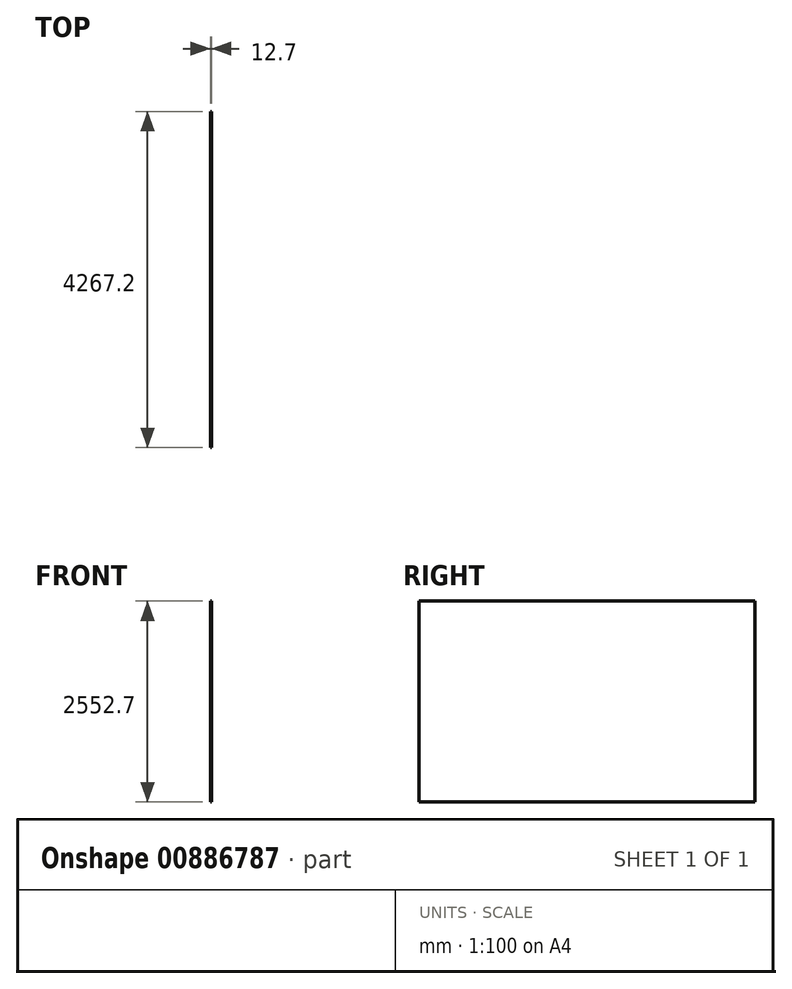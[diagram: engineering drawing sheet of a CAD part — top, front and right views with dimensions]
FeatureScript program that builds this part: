
annotation { "Feature Type Name" : "Feature", "Feature Type Description" : "" }
export const myFeature = defineFeature(function(context is Context, id is Id, definition is map)
    precondition{}
    {
        {
            var Q0;
            Q0=qCreatedBy(makeId("Right.planeOp"),FACE);
            var sketch = newSketch(context, id + "F0", { "sketchPlane" : qUnion([Q0])});
            skLineSegment(sketch, "E0.bottom", {"start": v(-2133.6, 1276.35) * mm, "end": v(2133.6, 1276.35) * mm});
            skLineSegment(sketch, "E0.top", {"start": v(-2133.6, -1276.35) * mm, "end": v(2133.6, -1276.35) * mm});
            skLineSegment(sketch, "E0.left", {"start": v(-2133.6, 1276.35) * mm, "end": v(-2133.6, -1276.35) * mm});
            skLineSegment(sketch, "E0.right", {"start": v(2133.6, 1276.35) * mm, "end": v(2133.6, -1276.35) * mm});
            skPoint(sketch, "E0.middle", {"position": v(0, 0) * mm});
            skSolve(sketch);
        }
        {
            var Q0;
            Q0=qSketchRegion(id+"F0",true);
            extrude(context, id + "F1", {"entities" : qUnion([Q0]), "depth" : 12.7 * mm, "offsetDistance" : 25.4 * mm});
        }
    });
